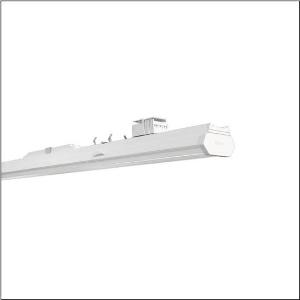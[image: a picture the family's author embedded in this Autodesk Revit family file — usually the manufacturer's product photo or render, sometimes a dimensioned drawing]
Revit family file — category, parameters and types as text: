
# Revit family: licross_r__21_protected_ho_52td1bmn4exm_7a17
name_source: partatom
category: Lighting Fixtures
units: mm (PartAtom-declared; Revit-internal decimal feet)

## family parameters
Cut with Voids When Loaded = No
Host = Face
Light Source = No
Part Type = Normal
Room Calculation Point = No
Round Connector Dimension = Use Diameter
Shared = No

## types (1)
- --- (1 x LED, 14040 lm, 83.2 W, 4000K)
    Apparent Load = 83 VA
    CIE Flux Codes = 54 82 95 97 100
    Color Rendering = 80
    Color Temperature = 4000K
    Default Elevation = 1800 mm
    Description = Licross® 21 Protected HO, luminaire insert, of sheet steel, galvanised, coil coated, white, length: 1.500mm, width: 90mm, height: 103mm, LED rated luminous flux: 14.040lm, light colour: 840, SDCM (Standard Deviation of Colour Matching)MacAdam ≤ 3 SDCM (initial), control gear: ON/OFF Multilumen, with plug, 3-pole, with phase selection, mains connection: 220..240V, AC, 50/60Hz, rated input power: 83W, internal wiring halogen-free, primary optical cover: cover, of PMMA, light emission: direct distribution, primary light characteristic: symmetric, protection rating (complete): IP54, insulation class (complete): insulation class I (protective earthing), certification: CE, ENEC, VDE, UKCA, protection symbol: D if used in an environment with non-conductive dust loads with corresponding accessories, impact resistance: IK06, permissible ambient temperature for indoor applications: -35..+35°C, corresponds to IFS (International Featured Standards) requirements for safety and quality in the food industry, reducing of maximum allowable ambient temperature of 5°C with ceiling mounting, LABS conformity tested according to VDMA 24364:2018-05, packaging unit: 1 piece
    Height = 92 mm
    Lamp = 1 x LED
    Lamp Light Flux = 14040 lm
    Lamp Power = 83.2 W
    Lamp count = 1
    Length = 1500 mm
    Luminous efficacy = 169 lm/W
    Manufacturer = Siteco
    ModVariant = No
    Model = 52TD1BMN4EXM
    Mounting Place = Ceiling
    Mounting Type = Pendant
    Number of Poles = 1
    OnlyDefault = Yes
    Power Factor = 1
    Product Name = Licross® 21 Protected HO
    Product group = luminaire insert | ceiling pendant
    ProductGroupID = 901
    Protection Class = Protection class I
    Protection Degree = IP 54
    RLX_Detail_Level = 1
    RLX_Emergency_Light_Flux = 0 lm
    RLX_Emergency_Type = 0
    RLX_Emergency_Type_DB = No
    RlxData = <blob elided: 22045 chars, md5=5d90420b>
    Socket = socket
    Standby Power = 0 W
    System Light Flux = 14040 lm
    System Power = 83 W
    Type Comments = factory setting: luminous flux: 100 % | (A | C | E) | 195 mA
    Type Image = l_1256148.jpg
    URL = http://relux.com
    VarID = @adj_113111
    Voltage = 0 V
    Weight = 0.00 kg
    Width = 88 mm

## geometry (parser evidence)
native form markers: Blend x4, Sweep x11
no freeform markers — native parametric forms only
